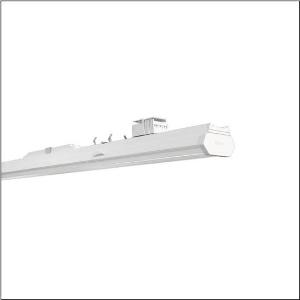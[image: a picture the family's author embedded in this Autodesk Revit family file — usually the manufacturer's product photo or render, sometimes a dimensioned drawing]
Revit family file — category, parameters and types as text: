
# Revit family: licross_r__21_protected_mo_52td1bvn455g_6e17
name_source: partatom
category: Lighting Fixtures
units: mm (PartAtom-declared; Revit-internal decimal feet)

## family parameters
Cut with Voids When Loaded = No
Host = Face
Light Source = No
Part Type = Normal
Room Calculation Point = No
Round Connector Dimension = Use Diameter
Shared = No

## types (1)
- --- (1 x LED, 5500 lm, 32.3 W, 4000K)
    Apparent Load = 32 VA
    CIE Flux Codes = 54 82 95 97 100
    Color Rendering = 80
    Color Temperature = 4000K
    Default Elevation = 1800 mm
    Description = Licross® 21 Protected MO, luminaire insert, of sheet steel, galvanised, coil coated, white, length: 1.500mm, width: 90mm, height: 101mm, LED rated luminous flux: 5.500lm, light colour: 840, control gear: DALI 2, CLO, with plug, 5-pole, with phase selection, mains connection: 220..240V, AC, 50/60Hz, start of lifetime: 32W, end of service life: 38W, halogen-free wiring, primary optical cover: cover, of PMMA, light emission: direct distribution, primary light characteristic: symmetric, protection rating (complete): IP54, insulation class (complete): insulation class I (protective earthing), certification: CE, ENEC, VDE, UKCA, protection symbol: D if used in an environment with non-conductive dust loads with corresponding accessories, impact resistance: IK06, permissible ambient temperature for indoor applications: -25..+45°C, corresponds to IFS (International Featured Standards) requirements for safety and quality in the food industry, reducing of maximum allowable ambient temperature of 5°C with ceiling mounting, LABS conformity tested according to VDMA 24364:2018-05, packaging unit: 1 piece
    Height = 92 mm
    Lamp = 1 x LED
    Lamp Light Flux = 5500 lm
    Lamp Power = 32.3 W
    Lamp count = 1
    Length = 1500 mm
    Luminous efficacy = 170 lm/W
    Manufacturer = Siteco
    ModVariant = No
    Model = 52TD1BVN455G
    Mounting Place = Ceiling
    Mounting Type = Pendant
    Number of Poles = 1
    OnlyDefault = Yes
    Power Factor = 1
    Product Name = Licross® 21 Protected MO
    Product group = luminaire insert
    ProductGroupID = 901
    Protection Class = Protection class I
    Protection Degree = IP 54
    RLX_Detail_Level = 1
    RLX_Emergency_Light_Flux = 0 lm
    RLX_Emergency_Type = 0
    RLX_Emergency_Type_DB = No
    RlxData = <blob elided: 23917 chars, md5=0c10bed6>
    Socket = socket
    Standby Power = 0 W
    System Light Flux = 5500 lm
    System Power = 32 W
    Type Comments = factory setting: luminous flux: 100 % | dim-lin: 254 | 219 mA
    Type Image = l_1256148.jpg
    URL = http://relux.com
    VarID = @adj_052105
    Voltage = 0 V
    Weight = 0.00 kg
    Width = 88 mm

## geometry (parser evidence)
native form markers: Blend x4, Sweep x10
no freeform markers — native parametric forms only
